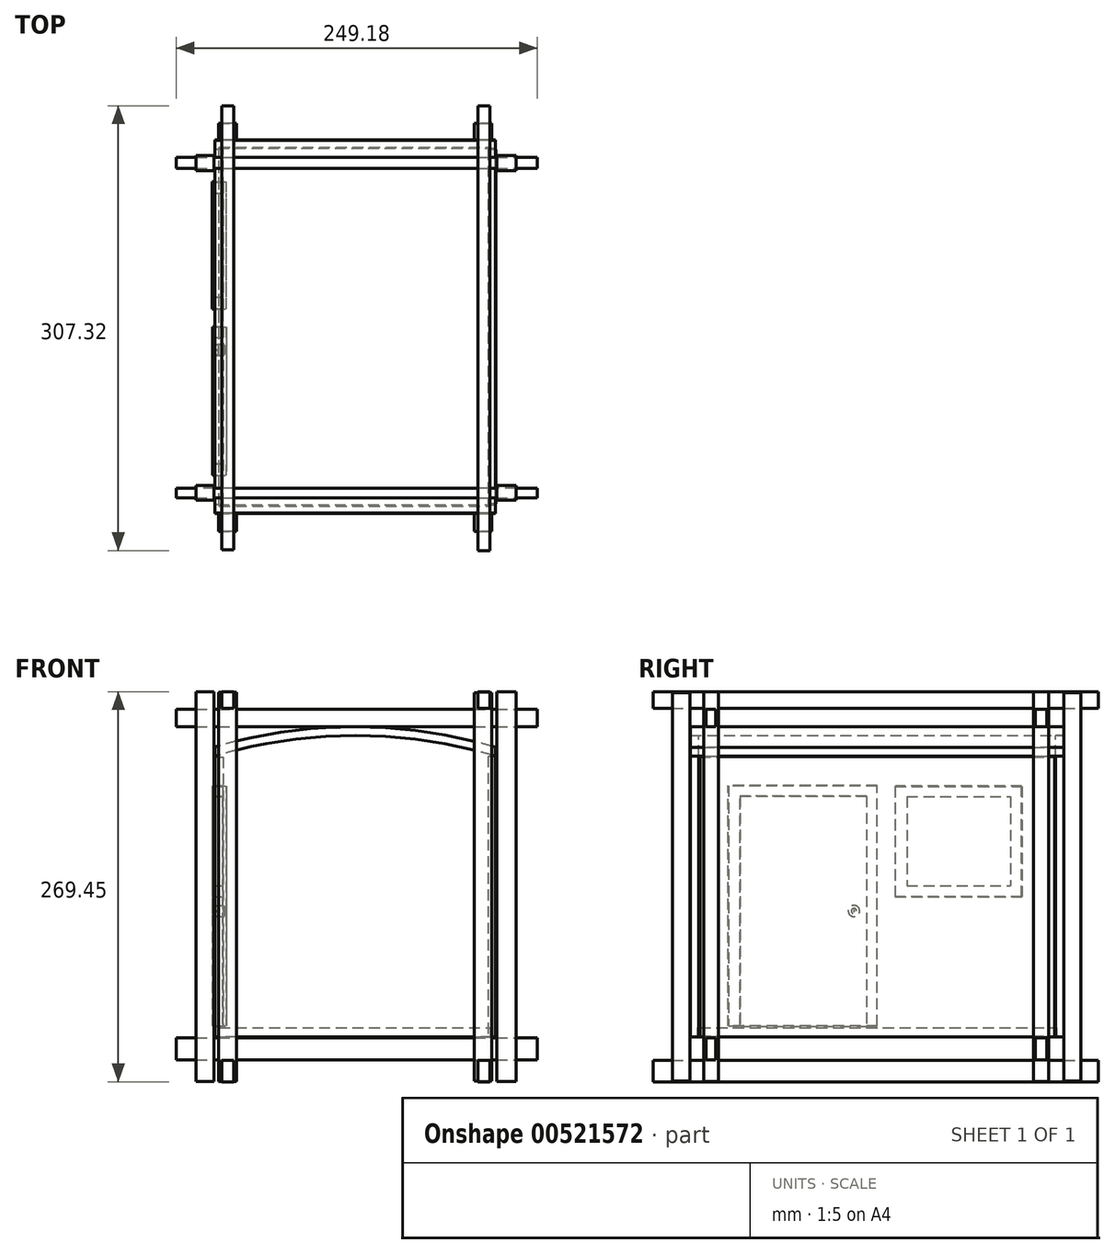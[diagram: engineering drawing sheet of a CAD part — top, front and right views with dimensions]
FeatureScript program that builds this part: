
annotation { "Feature Type Name" : "Feature", "Feature Type Description" : "" }
export const myFeature = defineFeature(function(context is Context, id is Id, definition is map)
    precondition{}
    {
        {
            var Q0;
            Q0=qCreatedBy(makeId("Front.planeOp"),FACE);
            var sketch = newSketch(context, id + "F0", { "sketchPlane" : qUnion([Q0])});
            skLineSegment(sketch, "E0", {"start": v(97.04, 97.04) * mm, "end": v(97.04, -96.89) * mm});
            skLineSegment(sketch, "E1", {"start": v(97.04, -96.89) * mm, "end": v(-96.89, -96.89) * mm});
            skLineSegment(sketch, "E2", {"start": v(-96.89, 97.04) * mm, "end": v(-96.89, -96.89) * mm});
            skArc(sketch, "E3", {"start": v(97.04, 97.04) * mm, "mid": v(0.08, 111.29) * mm, "end": v(-96.89, 97.04) * mm});
            skLineSegment(sketch, "E4", {"start": v(-96.89, 103.37) * mm, "end": v(-96.89, 97.04) * mm});
            skPoint(sketch, "E5.startSnap0", {"position": v(0.08, 111.29) * mm});
            skArc(sketch, "E6", {"start": v(97.04, 103.19) * mm, "mid": v(0.09, 117.3) * mm, "end": v(-96.89, 103.37) * mm});
            skLineSegment(sketch, "E7", {"start": v(97.04, 103.19) * mm, "end": v(97.04, 97.04) * mm});
            skSolve(sketch);
        }
        {
            var Q0;
            Q0=qCreatedBy(makeId("Right.planeOp"),FACE);
            var sketch = newSketch(context, id + "F1", { "sketchPlane" : qUnion([Q0])});
            skLineSegment(sketch, "E8.bottom", {"start": v(-124, 96.59) * mm, "end": v(124, 96.59) * mm});
            skLineSegment(sketch, "E8.top", {"start": v(-124, -96.59) * mm, "end": v(124, -96.59) * mm});
            skLineSegment(sketch, "E8.left", {"start": v(-124, 96.59) * mm, "end": v(-124, -96.59) * mm});
            skLineSegment(sketch, "E8.right", {"start": v(124, 96.59) * mm, "end": v(124, -96.59) * mm});
            skPoint(sketch, "E8.middle", {"position": v(0, 0) * mm});
            skLineSegment(sketch, "E9.bottom", {"start": v(100.14, 0) * mm, "end": v(11.51, 0) * mm});
            skLineSegment(sketch, "E9.top", {"start": v(100.14, 76.42) * mm, "end": v(11.51, 76.42) * mm});
            skLineSegment(sketch, "E9.left", {"start": v(100.14, 0) * mm, "end": v(100.14, 76.42) * mm});
            skLineSegment(sketch, "E9.right", {"start": v(11.51, 0) * mm, "end": v(11.51, 76.42) * mm});
            skLineSegment(sketch, "E10.bottom", {"start": v(17.87, 69.87) * mm, "end": v(93.79, 69.87) * mm});
            skLineSegment(sketch, "E10.top", {"start": v(17.87, 6.55) * mm, "end": v(93.79, 6.55) * mm});
            skLineSegment(sketch, "E10.left", {"start": v(17.87, 69.87) * mm, "end": v(17.87, 6.55) * mm});
            skLineSegment(sketch, "E10.right", {"start": v(93.79, 69.87) * mm, "end": v(93.79, 6.55) * mm});
            skPoint(sketch, "E10.middle", {"position": v(55.83, 38.21) * mm});
            skSolve(sketch);
        }
        {
            var Q0;
            Q0=makeQuery(id+"F0.imprint","IMPRINT",FACE,{"disambiguationData":[TD([[makeQuery(id+"F0.imprint","IMPRINT",EDGE,{"derivedFrom":sQuery(id+"F0.wireOp",EDGE,"E0")}),-1.0]])]});
            var sketch = newSketch(context, id + "F2", { "sketchPlane" : qUnion([Q0])});
            skSolve(sketch);
        }
        {
            var Q0;
            Q0=makeQuery(id+"F0.imprint","IMPRINT",FACE,{"disambiguationData":[TD([[makeQuery(id+"F0.imprint","IMPRINT",EDGE,{"derivedFrom":sQuery(id+"F0.wireOp",EDGE,"E0")}),-1.0]])]});
            extrude(context, id + "F3", {"entities" : qUnion([Q0]), "oppositeDirection" : true, "depth" : 128.86 * mm, "offsetDistance" : 25.4 * mm, "hasSecondDirection" : true, "secondDirectionOppositeDirection" : true, "secondDirectionDepth" : 123.07 * mm});
        }
        {
            var Q0;
            Q0=qCreatedBy(makeId("Top.planeOp"),FACE);
            var sketch = newSketch(context, id + "F4", { "sketchPlane" : qUnion([Q0])});
            skLineSegment(sketch, "E11.bottom", {"start": v(-93.76, -123.94) * mm, "end": v(93.76, -123.94) * mm});
            skLineSegment(sketch, "E11.top", {"start": v(-93.76, 123.94) * mm, "end": v(93.76, 123.94) * mm});
            skLineSegment(sketch, "E11.left", {"start": v(-93.76, -123.94) * mm, "end": v(-93.76, 123.94) * mm});
            skLineSegment(sketch, "E11.right", {"start": v(93.76, -123.94) * mm, "end": v(93.76, 123.94) * mm});
            skPoint(sketch, "E11.middle", {"position": v(0, 0) * mm});
            skSolve(sketch);
        }
        {
            var Q0;
            Q0=makeQuery(id+"F4.imprint","IMPRINT",FACE,{"disambiguationData":[TD([[makeQuery(id+"F4.imprint","IMPRINT",EDGE,{"derivedFrom":sQuery(id+"F4.wireOp",EDGE,"E11.bottom")}),1.0]])]});
            extrude(context, id + "F5", {"entities" : qUnion([Q0]), "oppositeDirection" : true, "depth" : 97.05 * mm, "offsetDistance" : 25.4 * mm, "hasSecondDirection" : true, "secondDirectionOppositeDirection" : true, "secondDirectionDepth" : 90.61 * mm});
        }
        {
            var Q0;
            Q0=makeQuery(id+"F0.imprint","IMPRINT",FACE,{"disambiguationData":[TD([[makeQuery(id+"F0.imprint","IMPRINT",EDGE,{"derivedFrom":sQuery(id+"F0.wireOp",EDGE,"E3")}),-1.0]])]});
            extrude(context, id + "F6", {"entities" : qUnion([Q0]), "depth" : 128.9 * mm, "offsetDistance" : 25.4 * mm, "hasSecondDirection" : true, "secondDirectionOppositeDirection" : true, "secondDirectionDepth" : 128.7 * mm});
        }
        {
            var Q0;
            Q0=makeQuery(id+"F2.imprint","IMPRINT",FACE,{"disambiguationData":[TD([[makeQuery(id+"F2.imprint","IMPRINT",EDGE,{"derivedFrom":makeQuery(id+"F0.imprint","IMPRINT",EDGE,{"derivedFrom":sQuery(id+"F0.wireOp",EDGE,"E0")})}),-1.0]])]});
            extrude(context, id + "F7", {"entities" : qUnion([Q0]), "depth" : 129.08 * mm, "offsetDistance" : 25.4 * mm, "hasSecondDirection" : true, "secondDirectionOppositeDirection" : false, "secondDirectionDepth" : 123.47 * mm});
        }
        {
            var Q0;
            Q0=qCreatedBy(makeId("Right.planeOp"),FACE);
            var sketch = newSketch(context, id + "F8", { "sketchPlane" : qUnion([Q0])});
            skLineSegment(sketch, "E12.bottom", {"start": v(122.43, 96.89) * mm, "end": v(-122.43, 96.89) * mm});
            skLineSegment(sketch, "E12.top", {"start": v(122.43, -96.89) * mm, "end": v(-122.43, -96.89) * mm});
            skLineSegment(sketch, "E12.left", {"start": v(122.43, 96.89) * mm, "end": v(122.43, -96.89) * mm});
            skLineSegment(sketch, "E12.right", {"start": v(-122.43, 96.89) * mm, "end": v(-122.43, -96.89) * mm});
            skPoint(sketch, "E12.middle", {"position": v(0, 0) * mm});
            skSolve(sketch);
        }
        {
            var Q0;
            Q0 = qSketchRegion(id + "F8", true);
            extrude(context, id + "F9", {"entities" : qUnion([Q0]), "depth" : 97.34 * mm, "offsetDistance" : 25.4 * mm, "hasSecondDirection" : true, "secondDirectionOppositeDirection" : false, "secondDirectionDepth" : 91.88 * mm});
        }
        {
            var Q0;
            Q0=qCreatedBy(makeId("Right.planeOp"),FACE);
            var sketch = newSketch(context, id + "F10", { "sketchPlane" : qUnion([Q0])});
            skLineSegment(sketch, "E13.bottom", {"start": v(-122.74, 96.39) * mm, "end": v(122.74, 96.39) * mm});
            skLineSegment(sketch, "E13.top", {"start": v(-122.74, -96.39) * mm, "end": v(122.74, -96.39) * mm});
            skLineSegment(sketch, "E13.left", {"start": v(-122.74, 96.39) * mm, "end": v(-122.74, -96.39) * mm});
            skLineSegment(sketch, "E13.right", {"start": v(122.74, 96.39) * mm, "end": v(122.74, -96.39) * mm});
            skPoint(sketch, "E13.middle", {"position": v(0, 0) * mm});
            skLineSegment(sketch, "E14.bottom", {"start": v(99.68, 0) * mm, "end": v(12.53, 0) * mm});
            skLineSegment(sketch, "E14.top", {"start": v(99.68, 76.43) * mm, "end": v(12.53, 76.43) * mm});
            skLineSegment(sketch, "E14.left", {"start": v(99.68, 0) * mm, "end": v(99.68, 76.43) * mm});
            skLineSegment(sketch, "E14.right", {"start": v(12.53, 0) * mm, "end": v(12.53, 76.43) * mm});
            skLineSegment(sketch, "E15.bottom", {"start": v(20.07, 69.11) * mm, "end": v(92.14, 69.11) * mm});
            skLineSegment(sketch, "E15.top", {"start": v(20.07, 7.32) * mm, "end": v(92.14, 7.32) * mm});
            skLineSegment(sketch, "E15.left", {"start": v(20.07, 69.11) * mm, "end": v(20.07, 7.32) * mm});
            skLineSegment(sketch, "E15.right", {"start": v(92.14, 69.11) * mm, "end": v(92.14, 7.32) * mm});
            skPoint(sketch, "E15.middle", {"position": v(56.1, 38.22) * mm});
            skLineSegment(sketch, "E16", {"start": v(0, 0) * mm, "end": v(0, -89.44) * mm});
            skLineSegment(sketch, "E17.bottom", {"start": v(0, -89.44) * mm, "end": v(-102.94, -89.44) * mm});
            skLineSegment(sketch, "E17.top", {"start": v(0, 76.65) * mm, "end": v(-102.94, 76.65) * mm});
            skLineSegment(sketch, "E17.left", {"start": v(0, -89.44) * mm, "end": v(0, 76.65) * mm});
            skLineSegment(sketch, "E17.right", {"start": v(-102.94, -89.44) * mm, "end": v(-102.94, 76.65) * mm});
            skSolve(sketch);
        }
        {
            var Q0;
            Q0=makeQuery(id+"F10.imprint","IMPRINT",FACE,{"disambiguationData":[TD([[makeQuery(id+"F10.imprint","IMPRINT",EDGE,{"derivedFrom":sQuery(id+"F10.wireOp",EDGE,"E13.bottom")}),-1.0]])]});
            extrude(context, id + "F11", {"entities" : qUnion([Q0]), "operationType" : NewBodyOperationType.ADD, "oppositeDirection" : true, "depth" : 96.6 * mm, "offsetDistance" : 25.4 * mm, "hasSecondDirection" : true, "secondDirectionOppositeDirection" : true, "secondDirectionDepth" : 90.9 * mm});
        }
        {
            var Q0;
            Q0=makeQuery(id+"F10.imprint","IMPRINT",FACE,{"disambiguationData":[TD([[makeQuery(id+"F10.imprint","IMPRINT",EDGE,{"derivedFrom":sQuery(id+"F10.wireOp",EDGE,"E14.bottom")}),-1.0]])]});
            var Q1;
            Q1 = qSketchRegion(id + "F10", true);
            extrude(context, id + "F12", {"entities" : qUnion([Q0, Q1]), "depth" : 25.4 * mm, "offsetDistance" : 25.4 * mm});
        }
        {
            var Q0;
            Q0=makeQuery(id+"F12.opExtrude","SWEPT_BODY",BODY,{"disambiguationData":[OSD([sQuery(id+"F10.wireOp",EDGE,"E13.bottom"),sQuery(id+"F10.wireOp",EDGE,"E13.top"),sQuery(id+"F10.wireOp",EDGE,"E13.left"),sQuery(id+"F10.wireOp",EDGE,"E13.right"),sQuery(id+"F10.wireOp",EDGE,"E15.bottom"),sQuery(id+"F10.wireOp",EDGE,"E15.top"),sQuery(id+"F10.wireOp",EDGE,"E15.left"),sQuery(id+"F10.wireOp",EDGE,"E15.right"),sQuery(id+"F10.wireOp",EDGE,"E17.bottom"),sQuery(id+"F10.wireOp",EDGE,"E17.top"),sQuery(id+"F10.wireOp",EDGE,"E17.left"),sQuery(id+"F10.wireOp",EDGE,"E17.right")])]});
            deleteBodies(context, id + "F13", {"entities" : qUnion([Q0])});
        }
        {
            var Q0;
            Q0=qCreatedBy(makeId("Right.planeOp"),FACE);
            var sketch = newSketch(context, id + "F14", { "sketchPlane" : qUnion([Q0])});
            skLineSegment(sketch, "E18.bottom", {"start": v(12.24, 76.08) * mm, "end": v(100.02, 76.08) * mm});
            skLineSegment(sketch, "E18.top", {"start": v(12.24, -0.18) * mm, "end": v(100.02, -0.18) * mm});
            skLineSegment(sketch, "E18.left", {"start": v(12.24, 76.08) * mm, "end": v(12.24, -0.18) * mm});
            skLineSegment(sketch, "E18.right", {"start": v(100.02, 76.08) * mm, "end": v(100.02, -0.18) * mm});
            skLineSegment(sketch, "E19.bottom", {"start": v(20.4, 68.99) * mm, "end": v(92.04, 68.99) * mm});
            skLineSegment(sketch, "E19.top", {"start": v(20.4, 7.45) * mm, "end": v(92.04, 7.45) * mm});
            skLineSegment(sketch, "E19.left", {"start": v(20.4, 68.99) * mm, "end": v(20.4, 7.45) * mm});
            skLineSegment(sketch, "E19.right", {"start": v(92.04, 68.99) * mm, "end": v(92.04, 7.45) * mm});
            skSolve(sketch);
        }
        {
            var Q0;
            Q0=makeQuery(id+"F14.imprint","IMPRINT",FACE,{"disambiguationData":[TD([[makeQuery(id+"F14.imprint","IMPRINT",EDGE,{"derivedFrom":sQuery(id+"F14.wireOp",EDGE,"E18.bottom")}),-1.0]])]});
            extrude(context, id + "F15", {"entities" : qUnion([Q0]), "oppositeDirection" : true, "depth" : 98.51 * mm, "offsetDistance" : 25.4 * mm, "hasSecondDirection" : true, "secondDirectionOppositeDirection" : true, "secondDirectionDepth" : 88.94 * mm});
        }
        {
            var Q0;
            Q0=qCreatedBy(makeId("Right.planeOp"),FACE);
            var sketch = newSketch(context, id + "F16", { "sketchPlane" : qUnion([Q0])});
            skLineSegment(sketch, "E20.bottom", {"start": v(-94.62, 69.34) * mm, "end": v(-7.44, 69.34) * mm});
            skLineSegment(sketch, "E20.top", {"start": v(-94.62, -89.54) * mm, "end": v(-7.44, -89.54) * mm});
            skLineSegment(sketch, "E20.left", {"start": v(-94.62, 69.34) * mm, "end": v(-94.62, -89.54) * mm});
            skLineSegment(sketch, "E20.right", {"start": v(-7.44, 69.34) * mm, "end": v(-7.44, -89.54) * mm});
            skPoint(sketch, "E20.middle", {"position": v(-51.03, -10.1) * mm});
            skSolve(sketch);
        }
        {
            var Q0;
            Q0=makeQuery(id+"F16.imprint","IMPRINT",FACE,{"disambiguationData":[TD([[makeQuery(id+"F16.imprint","IMPRINT",EDGE,{"derivedFrom":sQuery(id+"F16.wireOp",EDGE,"E20.bottom")}),-1.0]])]});
            extrude(context, id + "F17", {"entities" : qUnion([Q0]), "oppositeDirection" : true, "depth" : 96.36 * mm, "offsetDistance" : 25.4 * mm, "hasSecondDirection" : true, "secondDirectionOppositeDirection" : true, "secondDirectionDepth" : 91.7 * mm});
        }
        {
            var Q0;
            Q0=qCreatedBy(makeId("Right.planeOp"),FACE);
            var sketch = newSketch(context, id + "F18", { "sketchPlane" : qUnion([Q0])});
            skLineSegment(sketch, "E21", {"start": v(-0.3, -89.2) * mm, "end": v(-0.3, 76.5) * mm});
            skLineSegment(sketch, "E22", {"start": v(-0.3, 76.5) * mm, "end": v(-102.83, 76.5) * mm});
            skLineSegment(sketch, "E23", {"start": v(-102.83, 76.5) * mm, "end": v(-102.83, -89.33) * mm});
            skLineSegment(sketch, "E24", {"start": v(-102.83, -89.33) * mm, "end": v(-94.8, -89.33) * mm});
            skLineSegment(sketch, "E25", {"start": v(-94.8, -89.33) * mm, "end": v(-94.8, 69.34) * mm});
            skLineSegment(sketch, "E26", {"start": v(-7.57, 69.34) * mm, "end": v(-94.8, 69.34) * mm});
            skLineSegment(sketch, "E27", {"start": v(-7.57, 69.34) * mm, "end": v(-7.57, -89.2) * mm});
            skLineSegment(sketch, "E28", {"start": v(-7.57, -89.2) * mm, "end": v(-0.3, -89.2) * mm});
            skSolve(sketch);
        }
        {
            var Q0;
            Q0=makeQuery(id+"F18.imprint","IMPRINT",FACE,{"disambiguationData":[TD([[makeQuery(id+"F18.imprint","IMPRINT",EDGE,{"derivedFrom":sQuery(id+"F18.wireOp",EDGE,"E21")}),1.0]])]});
            extrude(context, id + "F19", {"entities" : qUnion([Q0]), "oppositeDirection" : true, "depth" : 98.47 * mm, "offsetDistance" : 25.4 * mm, "hasSecondDirection" : true, "secondDirectionOppositeDirection" : true, "secondDirectionDepth" : 88.82 * mm});
        }
        {
            var Q0;
            Q0=qCreatedBy(makeId("Right.planeOp"),FACE);
            var sketch = newSketch(context, id + "F20", { "sketchPlane" : qUnion([Q0])});
            skCircle(sketch, "E29", {"center": v(-16.12, -10) * mm, "radius": 3.9 * mm});
            skSolve(sketch);
        }
        {
            var Q0;
            Q0=makeQuery(id+"F20.imprint","IMPRINT",FACE,{"disambiguationData":[TD([[makeQuery(id+"F20.imprint","IMPRINT",EDGE,{"derivedFrom":sQuery(id+"F20.wireOp",EDGE,"E29")}),1.0]])]});
            var Q1;
            Q1 = qSketchRegion(id + "F2", true);
            extrude(context, id + "F21", {"entities" : qUnion([Q0, Q1]), "oppositeDirection" : true, "depth" : 98.42 * mm, "offsetDistance" : 25.4 * mm, "hasSecondDirection" : true, "secondDirectionOppositeDirection" : true, "secondDirectionDepth" : 89.62 * mm});
        }
        {
            var Q0;
            Q0=makeQuery(id+"F21.opExtrude","SWEPT_FACE",FACE,{"disambiguationData":[OSD([sQuery(id+"F20.wireOp",EDGE,"E29")])]});
            fillet(context, id + "F22", {"entities" : qUnion([Q0]), "radius" : 2.1 * mm, "tangentPropagation" : true, "allowEdgeOverflow" : false});
        }
        {
            var Q0;
            Q0=qCreatedBy(makeId("Right.planeOp"),FACE);
            var sketch = newSketch(context, id + "F23", { "sketchPlane" : qUnion([Q0])});
            skLineSegment(sketch, "E30", {"start": v(-120, 141.52) * mm, "end": v(-120, -127.79) * mm});
            skLineSegment(sketch, "E31", {"start": v(107.83, -127.79) * mm, "end": v(107.83, 141.52) * mm});
            skLineSegment(sketch, "E32", {"start": v(118.18, 141.52) * mm, "end": v(107.83, 141.52) * mm});
            skLineSegment(sketch, "E33", {"start": v(118.18, -127.79) * mm, "end": v(118.18, 141.52) * mm});
            skLineSegment(sketch, "E34", {"start": v(107.83, -127.79) * mm, "end": v(118.18, -127.79) * mm});
            skLineSegment(sketch, "E35", {"start": v(-109.65, 141.52) * mm, "end": v(-120, 141.52) * mm});
            skLineSegment(sketch, "E36", {"start": v(-109.65, -127.79) * mm, "end": v(-109.65, 141.52) * mm});
            skLineSegment(sketch, "E37", {"start": v(-120, -127.79) * mm, "end": v(-109.65, -127.79) * mm});
            skSolve(sketch);
        }
        {
            var Q0;
            Q0=makeQuery(id+"F23.imprint","IMPRINT",FACE,{"disambiguationData":[TD([[makeQuery(id+"F23.imprint","IMPRINT",EDGE,{"derivedFrom":sQuery(id+"F23.wireOp",EDGE,"E31")}),-1.0]])]});
            var Q1;
            Q1=makeQuery(id+"F23.imprint","IMPRINT",FACE,{"disambiguationData":[TD([[makeQuery(id+"F23.imprint","IMPRINT",EDGE,{"derivedFrom":sQuery(id+"F23.wireOp",EDGE,"E30")}),1.0]])]});
            extrude(context, id + "F24", {"entities" : qUnion([Q0, Q1]), "depth" : 111.1 * mm, "offsetDistance" : 25.4 * mm, "hasSecondDirection" : true, "secondDirectionOppositeDirection" : false, "secondDirectionDepth" : 97.8 * mm});
        }
        {
            var Q0;
            Q0 = qSketchRegion(id + "F23", true);
            extrude(context, id + "F25", {"entities" : qUnion([Q0]), "oppositeDirection" : true, "depth" : 109.74 * mm, "offsetDistance" : 25.4 * mm, "hasSecondDirection" : true, "secondDirectionOppositeDirection" : true, "secondDirectionDepth" : 97.35 * mm});
        }
        {
            var Q0;
            Q0=qCreatedBy(makeId("Front.planeOp"),FACE);
            var sketch = newSketch(context, id + "F26", { "sketchPlane" : qUnion([Q0])});
            skLineSegment(sketch, "E38", {"start": v(-94.12, -127.59) * mm, "end": v(-81.8, -127.59) * mm});
            skLineSegment(sketch, "E39", {"start": v(-94.12, 141.07) * mm, "end": v(-94.12, -127.59) * mm});
            skLineSegment(sketch, "E40", {"start": v(-81.8, 141.07) * mm, "end": v(-81.8, -127.59) * mm});
            skLineSegment(sketch, "E41", {"start": v(-81.8, 141.07) * mm, "end": v(-94.12, 141.07) * mm});
            skLineSegment(sketch, "E42", {"start": v(94.32, -127.39) * mm, "end": v(82.4, -127.39) * mm});
            skLineSegment(sketch, "E43", {"start": v(94.32, 140.88) * mm, "end": v(94.32, -127.39) * mm});
            skLineSegment(sketch, "E44", {"start": v(82.4, 140.88) * mm, "end": v(82.4, -127.39) * mm});
            skLineSegment(sketch, "E45", {"start": v(82.4, 140.88) * mm, "end": v(94.32, 140.88) * mm});
            skSolve(sketch);
        }
        {
            var Q0;
            Q0=makeQuery(id+"F26.imprint","IMPRINT",FACE,{"disambiguationData":[TD([[makeQuery(id+"F26.imprint","IMPRINT",EDGE,{"derivedFrom":sQuery(id+"F26.wireOp",EDGE,"E42")}),-1.0]])]});
            var Q1;
            Q1=makeQuery(id+"F26.imprint","IMPRINT",FACE,{"disambiguationData":[TD([[makeQuery(id+"F26.imprint","IMPRINT",EDGE,{"derivedFrom":sQuery(id+"F26.wireOp",EDGE,"E38")}),1.0]])]});
            extrude(context, id + "F27", {"entities" : qUnion([Q0, Q1]), "oppositeDirection" : true, "depth" : 140.48 * mm, "offsetDistance" : 25.4 * mm, "hasSecondDirection" : true, "secondDirectionOppositeDirection" : true, "secondDirectionDepth" : 128.89 * mm});
        }
        {
            var Q0;
            Q0 = qSketchRegion(id + "F26", true);
            extrude(context, id + "F28", {"entities" : qUnion([Q0]), "depth" : 141.5 * mm, "offsetDistance" : 25.4 * mm, "hasSecondDirection" : true, "secondDirectionOppositeDirection" : false, "secondDirectionDepth" : 129.24 * mm});
        }
        {
            var Q0;
            Q0=qCreatedBy(makeId("Top.planeOp"),FACE);
            var sketch = newSketch(context, id + "F29", { "sketchPlane" : qUnion([Q0])});
            skLineSegment(sketch, "E46", {"start": v(84.7, -154.81) * mm, "end": v(93.11, -154.81) * mm});
            skLineSegment(sketch, "E47", {"start": v(93.11, -154.81) * mm, "end": v(93.11, 152.5) * mm});
            skLineSegment(sketch, "E48", {"start": v(84.7, 152.5) * mm, "end": v(84.7, -154.81) * mm});
            skLineSegment(sketch, "E49", {"start": v(84.7, 152.5) * mm, "end": v(93.11, 152.5) * mm});
            skLineSegment(sketch, "E50", {"start": v(-92, -154.3) * mm, "end": v(-83.6, -154.3) * mm});
            skLineSegment(sketch, "E51", {"start": v(-92, -154.3) * mm, "end": v(-92, 152.5) * mm});
            skLineSegment(sketch, "E52", {"start": v(-83.6, 152.5) * mm, "end": v(-83.6, -154.3) * mm});
            skLineSegment(sketch, "E53", {"start": v(-92, 152.5) * mm, "end": v(-83.6, 152.5) * mm});
            skSolve(sketch);
        }
        {
            var Q0;
            Q0=makeQuery(id+"F29.imprint","IMPRINT",FACE,{"disambiguationData":[TD([[makeQuery(id+"F29.imprint","IMPRINT",EDGE,{"derivedFrom":sQuery(id+"F29.wireOp",EDGE,"E50")}),1.0]])]});
            var Q1;
            Q1=makeQuery(id+"F29.imprint","IMPRINT",FACE,{"disambiguationData":[TD([[makeQuery(id+"F29.imprint","IMPRINT",EDGE,{"derivedFrom":sQuery(id+"F29.wireOp",EDGE,"E46")}),1.0]])]});
            extrude(context, id + "F30", {"entities" : qUnion([Q0, Q1]), "depth" : 141.52 * mm, "offsetDistance" : 25.4 * mm, "hasSecondDirection" : true, "secondDirectionOppositeDirection" : false, "secondDirectionDepth" : 129.96 * mm});
        }
        {
            var Q0;
            Q0 = qSketchRegion(id + "F29", true);
            extrude(context, id + "F31", {"entities" : qUnion([Q0]), "oppositeDirection" : true, "depth" : 127.93 * mm, "offsetDistance" : 25.4 * mm, "hasSecondDirection" : true, "secondDirectionOppositeDirection" : true, "secondDirectionDepth" : 113.15 * mm});
        }
        {
            var Q0;
            Q0=qCreatedBy(makeId("Top.planeOp"),FACE);
            var sketch = newSketch(context, id + "F32", { "sketchPlane" : qUnion([Q0])});
            skLineSegment(sketch, "E54", {"start": v(-123.38, 109.18) * mm, "end": v(-123.38, 116.87) * mm});
            skLineSegment(sketch, "E55", {"start": v(-123.38, 116.87) * mm, "end": v(125.8, 116.87) * mm});
            skLineSegment(sketch, "E56", {"start": v(125.8, 116.87) * mm, "end": v(125.8, 109.18) * mm});
            skLineSegment(sketch, "E57", {"start": v(-123.38, 109.18) * mm, "end": v(125.8, 109.18) * mm});
            skLineSegment(sketch, "E58", {"start": v(125.8, -111.59) * mm, "end": v(-123.38, -111.59) * mm});
            skLineSegment(sketch, "E59", {"start": v(-123.38, -118.28) * mm, "end": v(125.8, -118.28) * mm});
            skLineSegment(sketch, "E60", {"start": v(125.8, -118.28) * mm, "end": v(125.8, -111.59) * mm});
            skLineSegment(sketch, "E61", {"start": v(-123.38, -111.59) * mm, "end": v(-123.38, -118.28) * mm});
            skSolve(sketch);
        }
        {
            var Q0;
            Q0=makeQuery(id+"F32.imprint","IMPRINT",FACE,{"disambiguationData":[TD([[makeQuery(id+"F32.imprint","IMPRINT",EDGE,{"derivedFrom":sQuery(id+"F32.wireOp",EDGE,"E54")}),-1.0]])]});
            var Q1;
            Q1=makeQuery(id+"F32.imprint","IMPRINT",FACE,{"disambiguationData":[TD([[makeQuery(id+"F32.imprint","IMPRINT",EDGE,{"derivedFrom":sQuery(id+"F32.wireOp",EDGE,"E58")}),1.0]])]});
            extrude(context, id + "F33", {"entities" : qUnion([Q0, Q1]), "oppositeDirection" : true, "depth" : 112.96 * mm, "offsetDistance" : 25.4 * mm, "hasSecondDirection" : true, "secondDirectionOppositeDirection" : true, "secondDirectionDepth" : 97.54 * mm});
        }
        {
            var Q0;
            Q0 = qSketchRegion(id + "F32", true);
            extrude(context, id + "F34", {"entities" : qUnion([Q0]), "depth" : 129.6 * mm, "offsetDistance" : 25.4 * mm, "hasSecondDirection" : true, "secondDirectionOppositeDirection" : false, "secondDirectionDepth" : 117.4 * mm});
        }
    });
